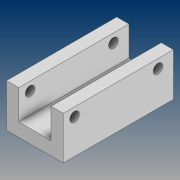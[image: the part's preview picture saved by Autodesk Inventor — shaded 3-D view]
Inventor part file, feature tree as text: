
AUTODESK INVENTOR PART (.ipt)
format: ipt  version: 2021 (Build 250183000, 183)  size: 101,888 bytes
history: native  units: mm
features: sketch x2, extrude x2, hole x1
ambient origin geometry x8: Origin, YZ Plane, XZ Plane, XY Plane, X Axis, Y Axis, Z Axis, Center Point
bodies: Solid1 (feature_tree)
feature tree (5):
  sketch  "Sketch1"  dims[d0=10.0mm d1=0.0mm d2=4.5mm d3=0.0mm]
  extrude  "Extrusion1"  Depth=4.5mm TaperAngle=0.0deg
  extrude  "Extrusion2"  [1 undecoded]
  hole  "Hole1"  [1 undecoded]
  sketch  "Sketch2"  dims[d4=3.2mm d5=6.0mm d6=4.0mm d7=2.0mm d8=90.0deg d9=8.0mm d10=20.594885mm]
note: 2 required parameter values undecoded (feature->parameter linkage not recoverable at this tier; creation-order binding heuristic only, values carry confidence <= 0.55)
